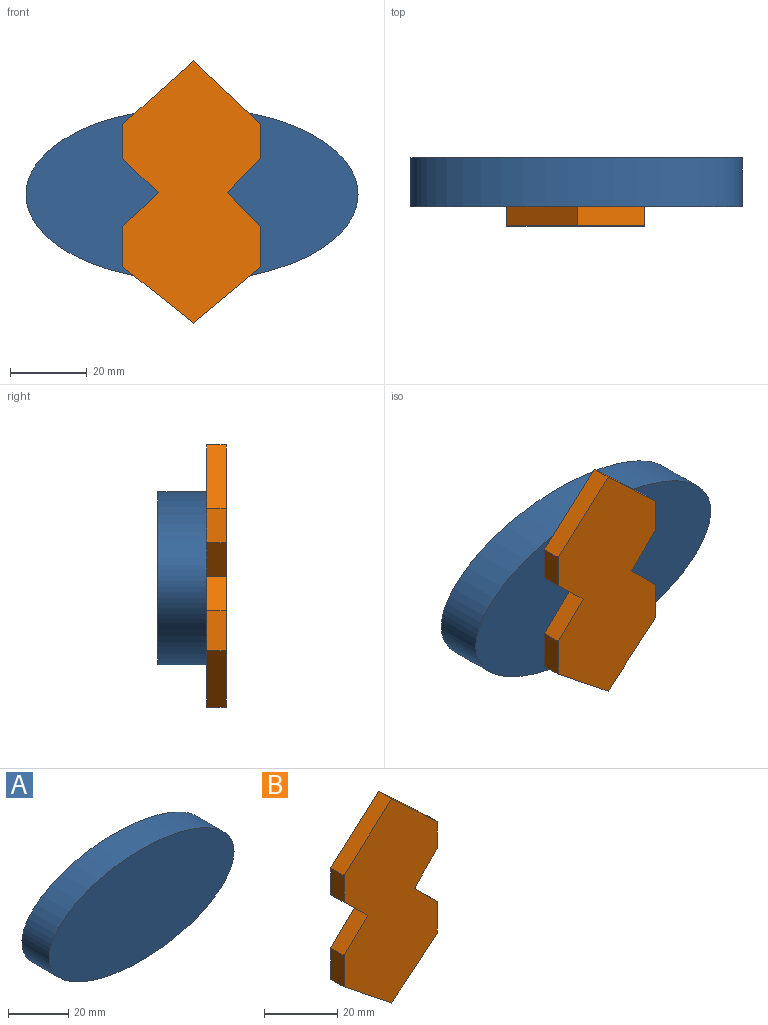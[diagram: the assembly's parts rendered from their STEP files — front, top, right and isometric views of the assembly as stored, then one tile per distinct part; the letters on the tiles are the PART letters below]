
ASSEMBLY  parts=2 mates=1
PART A: 3 faces, bbox 86.5x12.7x45.1 mm
  f0: extruded ~86.47x45.11mm, area 2690.2mm2, adj f1,f2
  f1: plane 86.47x45.11mm, normal (0,-1,0), area 3063.6mm2, adj f0
  f2: plane 86.47x45.11mm, normal (0,1,0), area 3063.6mm2, adj f0
PART B: 14 faces, bbox 35.9x5.1x68.2 mm
  f0: plane 8.87x8.75mm, normal (0.71,0,0.7), area 63.3mm2, adj f1,f11,f12,f13
  f1: plane 8.87x8.75mm, normal (0.71,0,-0.7), area 63.3mm2, adj f0,f2,f12,f13
  f2: plane 8.97x5.08mm, normal (1,0,0), area 45.6mm2, adj f1,f3,f12,f13
  f3: plane 17.51x16.45mm, normal (0.68,0,0.73), area 122mm2, adj f2,f4,f12,f13
  f4: plane 18.39x16.45mm, normal (-0.67,0,0.75), area 125.4mm2, adj f3,f5,f12,f13
  f5: plane 8.97x5.08mm, normal (-1,0,0), area 45.6mm2, adj f4,f6,f12,f13
  f6: plane 9.2x8.87mm, normal (-0.69,0,-0.72), area 64.9mm2, adj f5,f7,f12,f13
  f7: plane 9.2x8.87mm, normal (-0.69,0,0.72), area 64.9mm2, adj f6,f8,f12,f13
  f8: plane 10.47x5.08mm, normal (-1,0,0), area 53.2mm2, adj f7,f9,f12,f13
  f9: plane 18.39x14.6mm, normal (-0.62,0,-0.78), area 119.3mm2, adj f8,f10,f12,f13
  f10: plane 17.51x14.6mm, normal (0.64,0,-0.77), area 115.8mm2, adj f9,f11,f12,f13
  f11: plane 10.47x5.08mm, normal (1,0,0), area 53.2mm2, adj f0,f10,f12,f13
  f12: plane 68.22x35.9mm, normal (0,-1,0), area 1732.9mm2, adj f0,f1,f2,f3,f4,f5,f6,f7
  f13: plane 68.22x35.9mm, normal (0,1,0), area 1732.9mm2, adj f0,f1,f2,f3,f4,f5,f6,f7
PLACE A rot(axis=(0,-1,0),0deg) t=(-24.57,0.91,9.28)mm
PLACE B rot(axis=(0,-1,0),0deg) t=(-24.17,-11.79,-9.6)mm
MATE parallel B.f13 <-> A.f1  axis (0,1,0) through (-24.54,-11.79,9.48)mm
